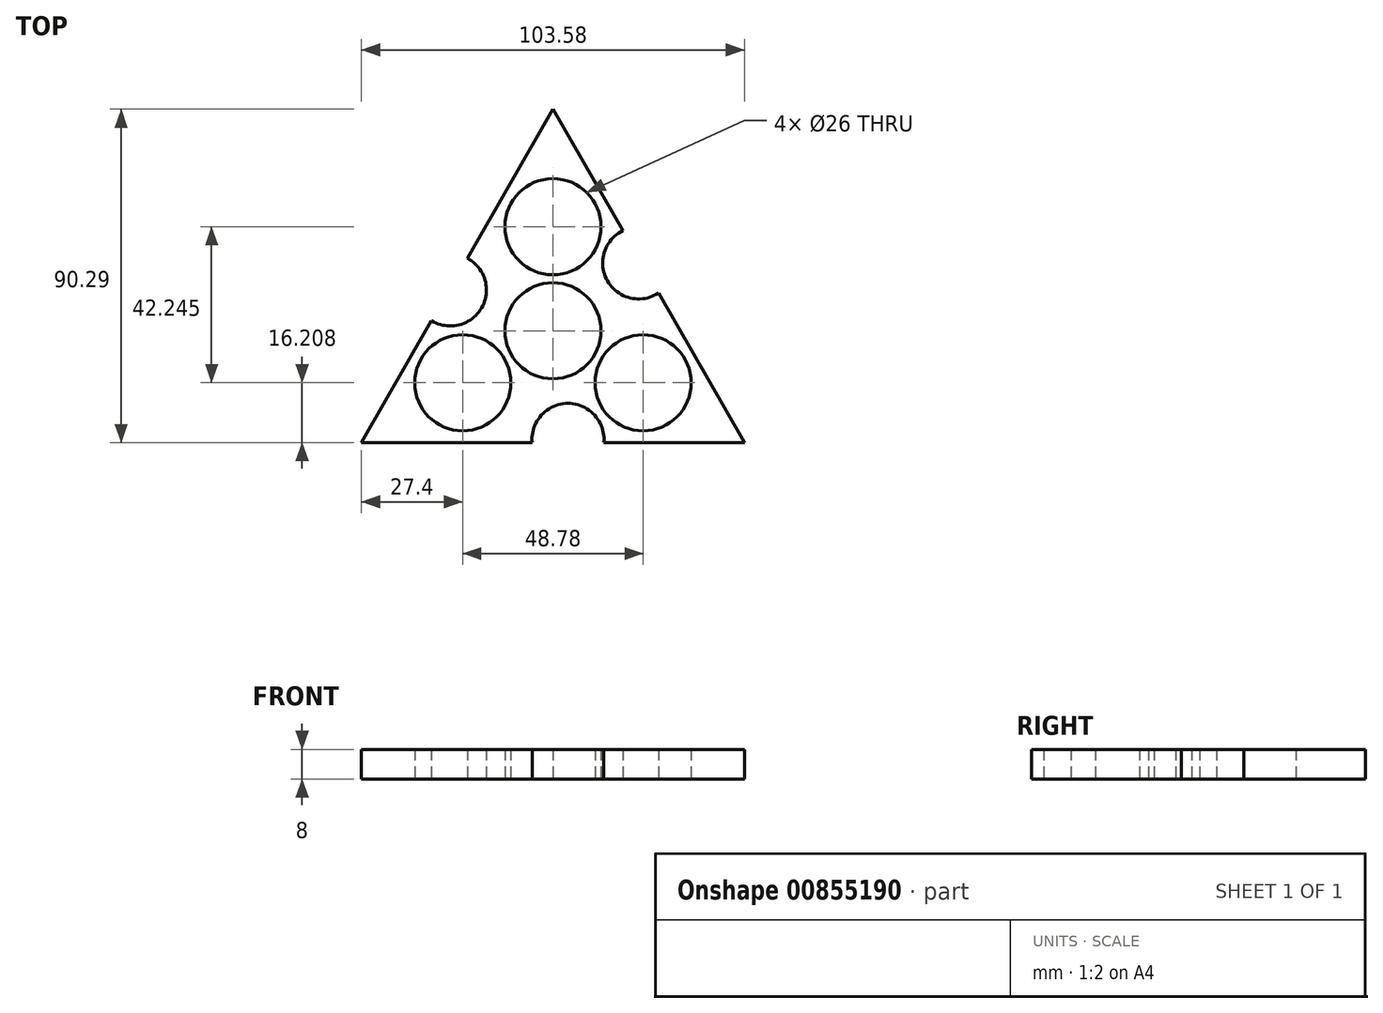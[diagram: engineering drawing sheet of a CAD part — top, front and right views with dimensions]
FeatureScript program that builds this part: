
annotation { "Feature Type Name" : "Feature", "Feature Type Description" : "" }
export const myFeature = defineFeature(function(context is Context, id is Id, definition is map)
    precondition{}
    {
        {
            var Q0;
            Q0=qCreatedBy(makeId("Top.planeOp"),FACE);
            var sketch = newSketch(context, id + "F0", { "sketchPlane" : qUnion([Q0])});
            skCircle(sketch, "E0", {"center": v(0, 0) * mm, "radius": 13 * mm});
            skCircle(sketch, "E1", {"center": v(0, 28.16) * mm, "radius": 13 * mm});
            skCircle(sketch, "E2.1.0", {"center": v(-24.4, -14.08) * mm, "radius": 13 * mm});
            skCircle(sketch, "E2.2.0", {"center": v(24.4, -14.08) * mm, "radius": 13 * mm});
            skPoint(sketch, "E3.center.orphan", {"position": v(-27.73, 11.04) * mm});
            skPoint(sketch, "E2.1.1.start.orphan", {"position": v(-39.9, -10.04) * mm});
            skPoint(sketch, "E4.end.orphan", {"position": v(-15.55, 32.13) * mm});
            skLineSegment(sketch, "E5", {"start": v(0, 60) * mm, "end": v(-23.15, 19.65) * mm});
            skLineSegment(sketch, "E6", {"start": v(-51.8, -30.3) * mm, "end": v(-5.64, -30.3) * mm});
            skLineSegment(sketch, "E7", {"start": v(51.8, -30.3) * mm, "end": v(28.55, 10.22) * mm});
            skArc(sketch, "E8", {"start": v(-32.84, 2.75) * mm, "mid": v(-19.27, 6.2) * mm, "end": v(-23.15, 19.65) * mm});
            skArc(sketch, "E9.1.0", {"start": v(13.77, -30.3) * mm, "mid": v(4.06, -19.65) * mm, "end": v(-5.64, -30.3) * mm});
            skArc(sketch, "E9.2.0", {"start": v(18.87, 27.1) * mm, "mid": v(14.74, 13.5) * mm, "end": v(28.55, 10.22) * mm});
            skPoint(sketch, "E9.center", {"position": v(-0.16, 0) * mm});
            skLineSegment(sketch, "E10.trimOffspring", {"start": v(-32.84, 2.75) * mm, "end": v(-51.8, -30.3) * mm});
            skLineSegment(sketch, "E11.trimOffspring", {"start": v(18.87, 27.1) * mm, "end": v(0, 60) * mm});
            skLineSegment(sketch, "E12.trimOffspring", {"start": v(13.77, -30.3) * mm, "end": v(51.8, -30.3) * mm});
            skCircle(sketch, "E13", {"center": v(0, 0) * mm, "radius": 60 * mm, "construction": true});
            skSolve(sketch);
        }
        {
            var Q0;
            Q0=makeQuery(id+"F0.imprint","IMPRINT",FACE,{"disambiguationData":[TD([[makeQuery(id+"F0.imprint","IMPRINT",EDGE,{"derivedFrom":sQuery(id+"F0.wireOp",EDGE,"E0")}),-1.0]])]});
            extrude(context, id + "F1", {"entities" : qUnion([Q0]), "depth" : 8 * mm, "offsetDistance" : 25 * mm});
        }
    });
